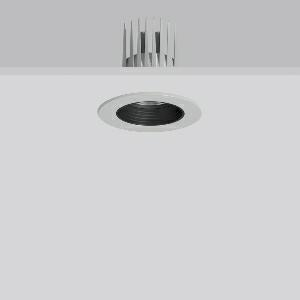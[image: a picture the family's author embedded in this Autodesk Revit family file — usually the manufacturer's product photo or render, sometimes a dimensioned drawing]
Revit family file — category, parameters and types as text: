
# Revit family: heledon_mini_e_901747_004_76_6d3f
name_source: partatom
category: Lighting Fixtures
units: mm (PartAtom-declared; Revit-internal decimal feet)

## family parameters
Cut with Voids When Loaded = No
Host = Face
Light Source = No
Part Type = Normal
Room Calculation Point = No
Round Connector Dimension = Use Diameter
Shared = No

## types (1)
- HELEDON mini E (1 x LED Modul 930, 1950 lm, 3000)
    Apparent Load = 20 VA
    Approval mark = CE
    CIE Flux Codes = 95 100 100 100 100
    Color Rendering = 90
    Color Temperature = 3000
    Default Elevation = 1800 mm
    Description = Series: HELEDON mini
Round recessed downlight. Housing: die-cast aluminium, powder-coated. Black plastic ring and recessed LED to prevent glare from the side. Optical assembly with lens made of plastic (polycarbonate) for the best homogeneous light distribution - can be changed without tools. Best colour rendering index Ra>90. Suitable for Recessed ceiling mounting. Installation without tools thanks to spring fastening system. Including separate LED converter with connecting cable 600 mm.High quality converter without flickering and stroboscopic effect. Through-wiring box (5 pole) available as accessory. The following accessories can be mounted without use of tools: interchangeable lenses, decorative glasses, honeycomb louvre, clear and frosted diffusers, white interchangeable plastic ring. 
Colour: silver
Diameter: 124 mm
Height: 3 mm
Cut-out diameter: 114 mm
Recess height: 170 mm
Luminaire: recess height: 120 mm
Lamp: LED
Socket: without socket
Colour temperature: 3000K
Colour rendering index (CRI): 92
System power: 20 W
Rated luminous flux: 1950 lm
Luminous efficiency: 98 lm/W
Control gear: Converter, dimmable, DALI
Protection class: II
Type of protection: IP 20
    Height = 0 mm  [stored 0 ft]
    Lamp = 1 x LED Modul 930
    Lamp Light Flux = 1950 lm
    Lamp count = 1
    Length = 124 mm  [stored 0.406824 ft]
    Lifetime = 50000 h
    Luminous efficacy = 98 lm/W
    Manufacturer = RZB
    ModVariant = No
    Model = 901747.004.76
    Mounting Place = Ceiling
    Mounting Type = Recessed
    Number of Poles = 1
    OnlyDefault = Yes
    Power Factor = 1
    Product Name = HELEDON mini E
    Product group = Recessed downlights
    ProductGroupID = 402
    Protection Class = Protection class II
    Protection Degree = IP 20
    RLX_Detail_Level = 1
    RLX_Emergency_Light_Flux = 0 lm
    RLX_Emergency_Type = 0
    RLX_Emergency_Type_DB = No
    RlxData = <blob elided: 134229 chars, md5=9736537b>
    Socket = socket
    Standby Power = 0 W
    System Light Flux = 1950 lm
    System Power = 20 W
    Type Comments = Product without accessories
    Type Image = 901656.004.jpg
    URL = http://relux.com
    VarID = ---
    Voltage = 230 V
    Voltage Range = 220-240 V
    Weight = 0.00 kg
    Width = 0 mm  [stored 0 ft]

note: [stored X ft] marks values corroborated as IEEE doubles in the binary element streams (Revit-internal decimal feet)

## geometry (parser evidence)
native form markers: Blend x4, Sweep x9
no freeform markers — native parametric forms only
